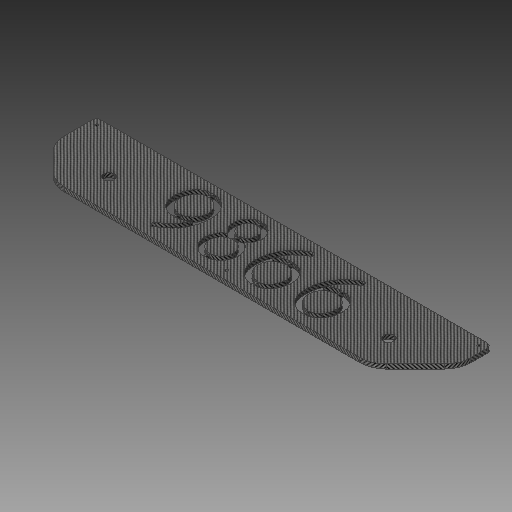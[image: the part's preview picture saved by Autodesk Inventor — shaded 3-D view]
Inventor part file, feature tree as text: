
AUTODESK INVENTOR PART (.ipt)
format: ipt  version: 2018.3 (Build 223284000, 284)  size: 696,832 bytes
history: native  units: mm
features: extrude x9, sketch x9, projected_geometry x3, fillet x1
ambient origin geometry x8: Origin, YZ Plane, XZ Plane, XY Plane, X Axis, Y Axis, Z Axis, Center Point
bodies: Solid1 (feature_tree), Body1 (feature_tree)
feature tree (22):
  extrude  "Extrusion1"  Depth=22.5mm
  extrude  "Extrusion2"  Depth=34.677mm
  extrude  "Extrusion3"  Depth=3.1mm
  fillet  "Fillet1"  Radius=7.5mm
  extrude  "Extrusion4"  Depth=10.0mm TaperAngle=0.0deg
  extrude  "Extrusion5"  Depth=3.1mm
  extrude  "Extrusion6"  Depth=7.5mm
  extrude  "Extrusion7"  Depth=7.5mm
  extrude  "Extrusion8"  Depth=5.0mm TaperAngle=0.0deg
  extrude  "Extrusion9"  Depth=10.0mm TaperAngle=0.0deg
  sketch  "Sketch1"  dims[d0=22.5mm d1=22.5mm]
  sketch  "Sketch2"  dims[d2=10.0mm d3=0.0mm d4=34.677mm]
  sketch  "Sketch3"  dims[d6=10.0mm d7=0.0mm d8=3.1mm d9=7.5mm]
  sketch  "Sketch4"  dims[d10=10.0mm d11=10.0mm d12=0.0mm]
  projected_geometry  "Projected Loop1"
  sketch  "Sketch5"  dims[d13=5.0mm d14=3.1mm]
  projected_geometry  "Projected Loop2"
  sketch  "Sketch6"  dims[d15=7.5mm d16=7.5mm]
  sketch  "Sketch7"  dims[d17=3.1mm d18=7.5mm]
  sketch  "Sketch8"  dims[d19=7.5mm d20=5.0mm d21=0.0mm]
  sketch  "Sketch9"  dims[d22=5.0mm d23=0.0mm d24=10.0mm d25=0.0mm d26=10.0mm d27=0.0mm d28=10.0mm d29=0.0mm d30=2.0mm d31=2.0mm d32=2.0mm d33=2.0mm d34=5.0mm d35=0.0mm]
  projected_geometry  "Projected Loop3"
